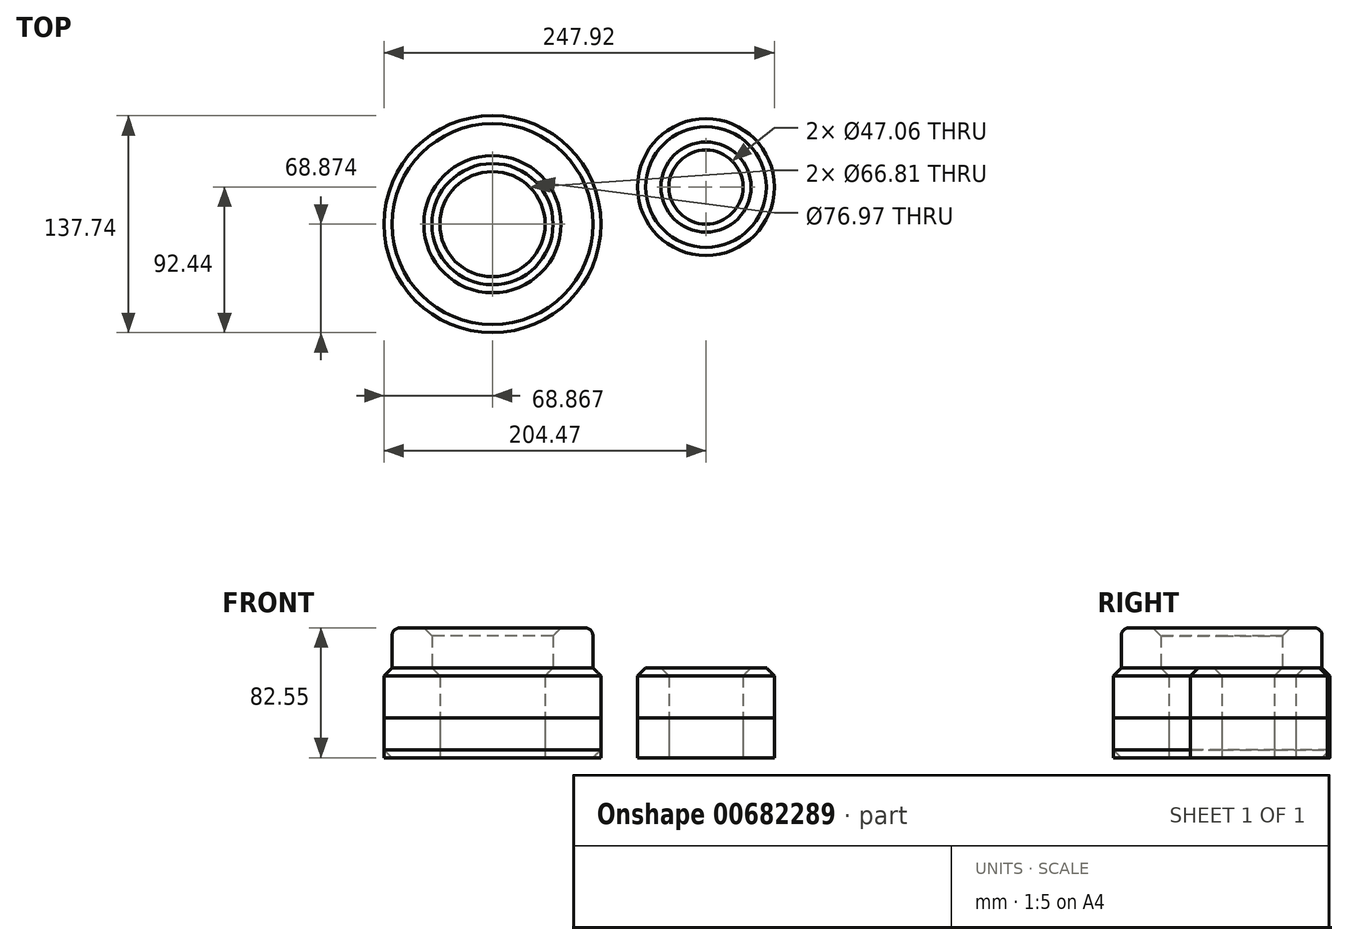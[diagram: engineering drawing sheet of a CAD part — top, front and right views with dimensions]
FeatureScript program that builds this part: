
annotation { "Feature Type Name" : "Feature", "Feature Type Description" : "" }
export const myFeature = defineFeature(function(context is Context, id is Id, definition is map)
    precondition{}
    {
        {
            var Q0;
            Q0=qCreatedBy(makeId("Top.planeOp"),FACE);
            var sketch = newSketch(context, id + "F0", { "sketchPlane" : qUnion([Q0])});
            skCircle(sketch, "E0", {"center": v(-135.6, -23.57) * mm, "radius": 68.87 * mm});
            skCircle(sketch, "E1", {"center": v(0, 0) * mm, "radius": 43.45 * mm});
            skCircle(sketch, "E2", {"center": v(-135.6, -23.57) * mm, "radius": 33.4 * mm});
            skCircle(sketch, "E3", {"center": v(0, 0) * mm, "radius": 23.53 * mm});
            skLineSegment(sketch, "E4", {"start": v(-132.84, 45.25) * mm, "end": v(0, 43.46) * mm});
            skLineSegment(sketch, "E5", {"start": v(14.02, -41.13) * mm, "end": v(-111.47, -88.07) * mm});
            skSolve(sketch);
        }
        {
            var Q0;
            Q0 = qSketchRegion(id + "F0", true);
            extrude(context, id + "F1", {"entities" : qUnion([Q0]), "depth" : 57.15 * mm, "offsetDistance" : 25.4 * mm});
        }
        {
            var Q0;
            Q0 = qSketchRegion(id + "F0", true);
            extrude(context, id + "F2", {"entities" : qUnion([Q0]), "depth" : 25.4 * mm, "offsetDistance" : 25.4 * mm});
        }
        {
            var Q0;
            Q0=makeQuery(id+"F1.opExtrude","SWEPT_FACE",FACE,{"disambiguationData":[OSD([sQuery(id+"F0.wireOp",EDGE,"E0")])]});
            var Q1;
            Q1=makeQuery(id+"F1.opExtrude","CAP_EDGE",EDGE,{"disambiguationData":[OSD([sQuery(id+"F0.wireOp",EDGE,"E2")])],"isStart":false});
            var Q2;
            Q2=makeQuery(id+"F1.opExtrude","CAP_EDGE",EDGE,{"disambiguationData":[OSD([sQuery(id+"F0.wireOp",EDGE,"E1")])],"isStart":false});
            var Q3;
            Q3=makeQuery(id+"F1.opExtrude","CAP_EDGE",EDGE,{"disambiguationData":[OSD([sQuery(id+"F0.wireOp",EDGE,"E3")])],"isStart":false});
            chamfer(context, id + "F3", {"entities" : qUnion([Q0, Q1, Q2, Q3]), "width" : 5.08 * mm, "tangentPropagation" : true});
        }
        {
            var Q0;
            Q0=makeQuery(id+"F1.opExtrude","CAP_FACE",FACE,{"disambiguationData":[OSD([sQuery(id+"F0.wireOp",EDGE,"E0"),sQuery(id+"F0.wireOp",EDGE,"E2")])],"isStart":false});
            extrude(context, id + "F4", {"entities" : qUnion([Q0]), "operationType" : NewBodyOperationType.ADD, "depth" : 25.4 * mm, "offsetDistance" : 25.4 * mm});
        }
        {
            var Q0;
            {var subQ0=sQuery(id+"F0.wireOp",EDGE,"E2");var subQ1=sQuery(id+"F0.wireOp",EDGE,"E0");Q0=makeQuery(id+"F4.opExtrude","CAP_EDGE",EDGE,{"disambiguationData":[OSD([subQ1,subQ0]),TDD([makeQuery(id+"F3.opChamfer","BLEND_EDGE",EDGE,{"blendedFrom":[makeQuery(id+"F1.opExtrude","CAP_EDGE",EDGE,{"disambiguationData":[OSD([subQ1])],"isStart":false}),makeQuery(id+"F1.opExtrude","CAP_FACE",FACE,{"disambiguationData":[OSD([subQ1,subQ0])],"isStart":false})],"blendedInto":[makeQuery(id+"F1.opExtrude","CAP_FACE",FACE,{"disambiguationData":[OSD([subQ1,subQ0])],"isStart":false})]})])],"isStart":false});}
            fillet(context, id + "F5", {"entities" : qUnion([Q0]), "tangentPropagation" : true, "radius" : 5.08 * mm, "defaultsChanged" : false, "vertexSettings" : [], "allowEdgeOverflow" : false});
        }
        {
            var Q0;
            {var subQ0=sQuery(id+"F0.wireOp",EDGE,"E2");var subQ1=sQuery(id+"F0.wireOp",EDGE,"E0");Q0=makeQuery(id+"F4.opExtrude","CAP_EDGE",EDGE,{"disambiguationData":[OSD([subQ1,subQ0]),TDD([makeQuery(id+"F3.opChamfer","BLEND_EDGE",EDGE,{"blendedFrom":[makeQuery(id+"F1.opExtrude","CAP_EDGE",EDGE,{"disambiguationData":[OSD([subQ0])],"isStart":false}),makeQuery(id+"F1.opExtrude","CAP_FACE",FACE,{"disambiguationData":[OSD([subQ1,subQ0])],"isStart":false})],"blendedInto":[makeQuery(id+"F1.opExtrude","CAP_FACE",FACE,{"disambiguationData":[OSD([subQ1,subQ0])],"isStart":false})]})])],"isStart":false});}
            chamfer(context, id + "F6", {"entities" : qUnion([Q0]), "width" : 5.08 * mm, "tangentPropagation" : true});
        }
    });
